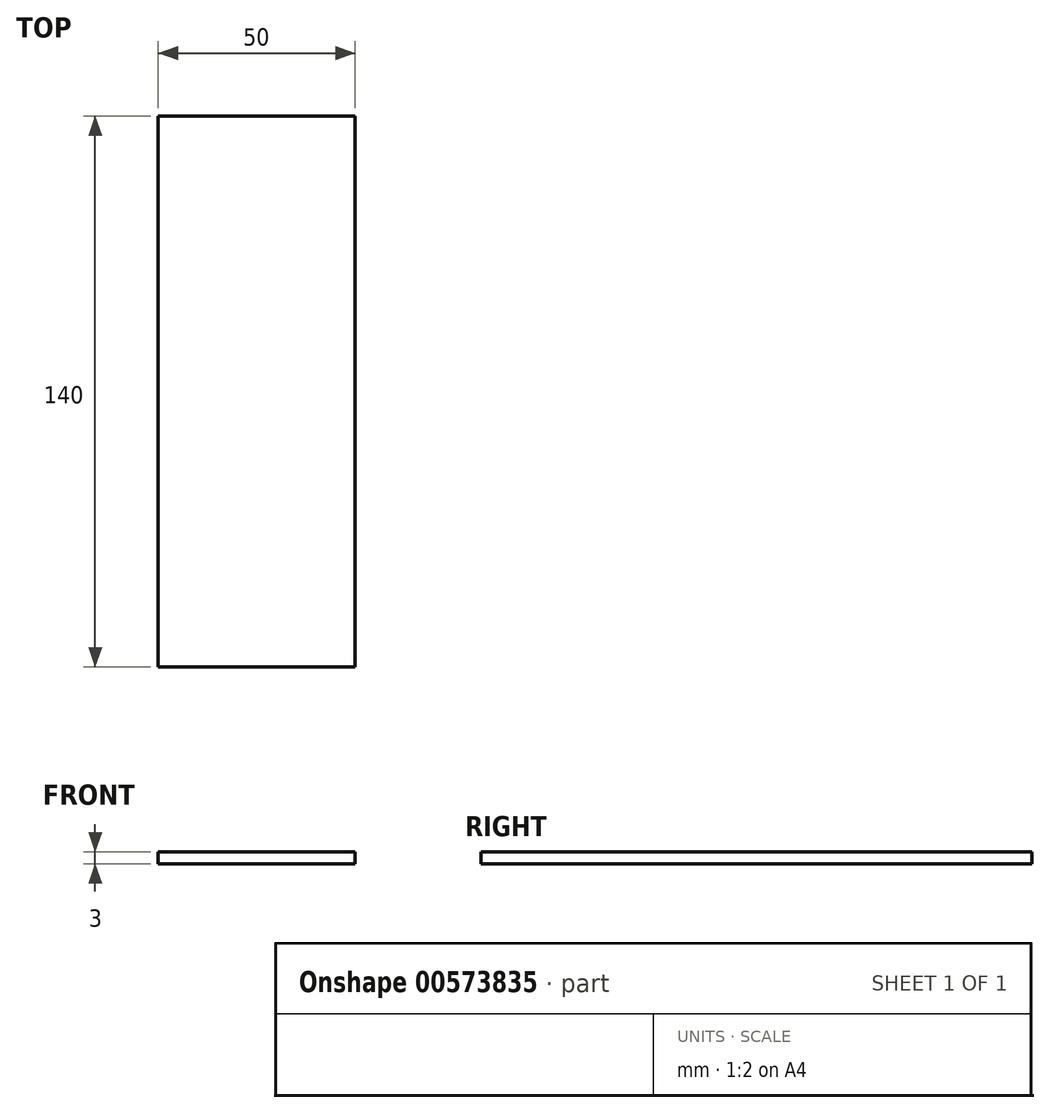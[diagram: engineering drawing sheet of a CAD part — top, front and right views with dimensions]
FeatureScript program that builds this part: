
annotation { "Feature Type Name" : "Feature", "Feature Type Description" : "" }
export const myFeature = defineFeature(function(context is Context, id is Id, definition is map)
    precondition{}
    {
        {
            var Q0;
            Q0=qCreatedBy(makeId("Top.planeOp"),FACE);
            var sketch = newSketch(context, id + "F0", { "sketchPlane" : qUnion([Q0])});
            skLineSegment(sketch, "E0.bottom", {"start": v(0, 0) * mm, "end": v(50, 0) * mm});
            skLineSegment(sketch, "E0.top", {"start": v(0, 140) * mm, "end": v(50, 140) * mm});
            skLineSegment(sketch, "E0.left", {"start": v(0, 0) * mm, "end": v(0, 140) * mm});
            skLineSegment(sketch, "E0.right", {"start": v(50, 0) * mm, "end": v(50, 140) * mm});
            skSolve(sketch);
        }
        {
            var Q0;
            Q0=makeQuery(id+"F0.imprint","IMPRINT",FACE,{"disambiguationData":[TD([[makeQuery(id+"F0.imprint","IMPRINT",EDGE,{"derivedFrom":sQuery(id+"F0.wireOp",EDGE,"E0.bottom")}),1.0]])]});
            extrude(context, id + "F1", {"entities" : qUnion([Q0]), "depth" : 3 * mm, "offsetDistance" : 25 * mm});
        }
    });
